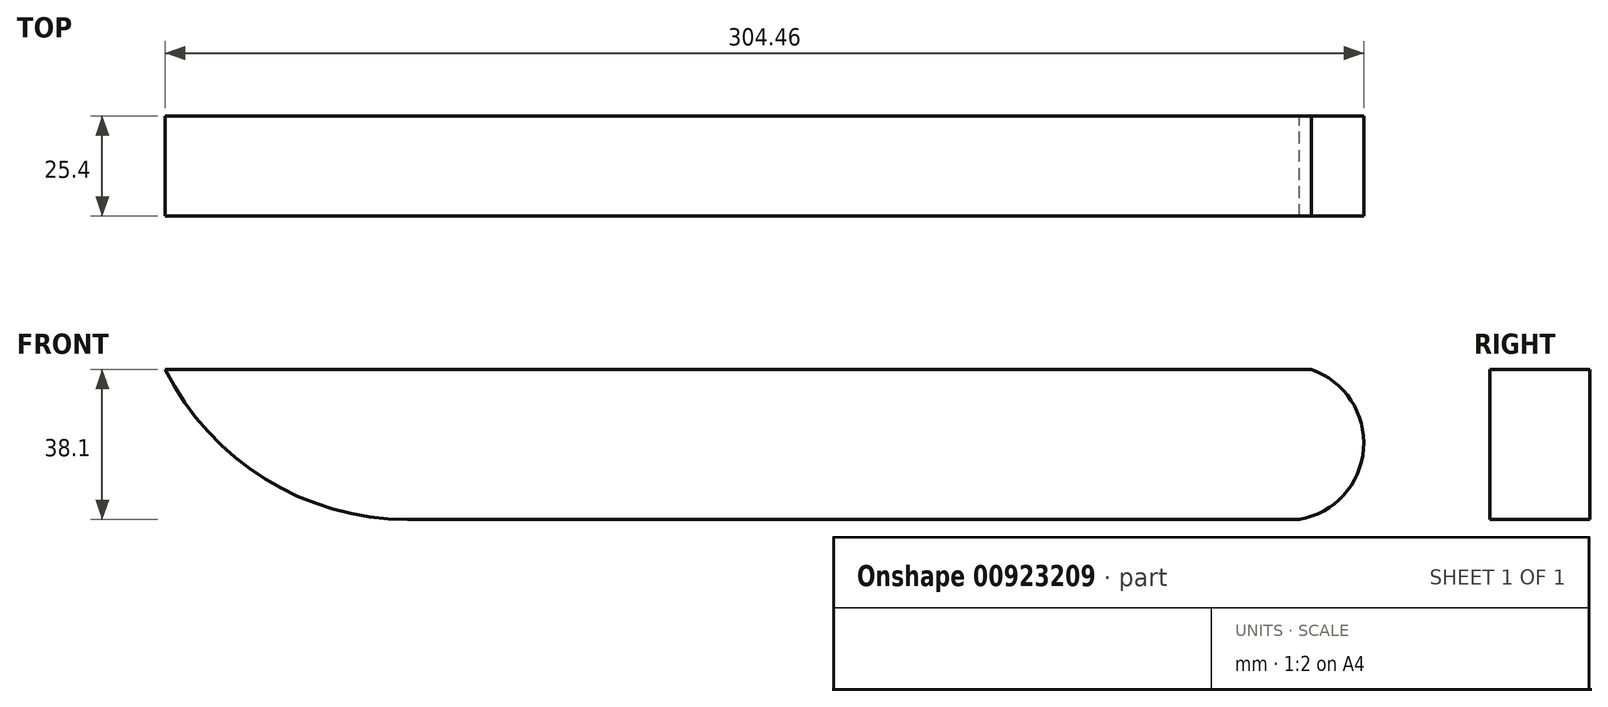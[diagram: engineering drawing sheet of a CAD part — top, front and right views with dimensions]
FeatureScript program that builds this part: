
annotation { "Feature Type Name" : "Feature", "Feature Type Description" : "" }
export const myFeature = defineFeature(function(context is Context, id is Id, definition is map)
    precondition{}
    {
        {
            var Q0;
            Q0=qCreatedBy(makeId("Front.planeOp"),FACE);
            var sketch = newSketch(context, id + "F0", { "sketchPlane" : qUnion([Q0])});
            skArc(sketch, "E0", {"start": v(-148.96, 18.87) * mm, "mid": v(-123.63, -8.93) * mm, "end": v(-87.46, -19.23) * mm});
            skArc(sketch, "E1", {"start": v(139.17, -19.23) * mm, "mid": v(155.44, -1.34) * mm, "end": v(142.16, 18.87) * mm});
            skLineSegment(sketch, "E2", {"start": v(-148.96, 18.87) * mm, "end": v(142.16, 18.87) * mm});
            skLineSegment(sketch, "E3", {"start": v(-87.46, -19.23) * mm, "end": v(139.17, -19.23) * mm});
            skSolve(sketch);
        }
        {
            var Q0;
            Q0 = qSketchRegion(id + "F0", true);
            extrude(context, id + "F1", {"entities" : qUnion([Q0]), "depth" : 25.4 * mm, "offsetDistance" : 25.4 * mm});
        }
    });
